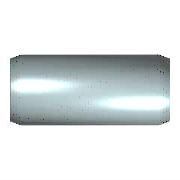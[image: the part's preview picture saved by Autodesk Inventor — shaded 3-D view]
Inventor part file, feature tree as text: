
AUTODESK INVENTOR PART (.ipt)
format: ipt  version: 2023.3 (Build 273359000, 359)  size: 163,328 bytes
history: native  units: mm (DEFAULTED — no unit token found)
features: sketch x5, extrude x3, plane x2, chamfer x1, hole x1, revolve x1
ambient origin geometry x8: Origin, YZ Plane, XZ Plane, XY Plane, X Axis, Y Axis, Z Axis, Center Point
bodies: Solid1 (feature_tree)
feature tree (13):
  extrude  "Körper"  Depth=16.0mm TaperAngle=0.0deg
  chamfer  "Skizze2"  Distance=0.5mm
  plane  "Arbeitsebene1"
  hole  "Bohrung1"  [1 undecoded]
  extrude  "Extrusion2"  TaperAngle=0.0deg  [1 undecoded]
  plane  "Arbeitsebene2"
  extrude  "Extrusion3"  TaperAngle=0.0deg  [1 undecoded]
  revolve  "Umdrehung1"
  sketch  "Skizze"  dims[d9=15.0deg d11=0.5mm d12=0.5mm d13=0.0mm d15=0.0mm d16=0.0mm d17=1.5mm d18=5.5mm d19=0.5mm d20=6.0mm d21=1.7mm d22=2.0mm d23=30.0deg d24=12.0mm d25=0.0mm d26=2.0mm d27=5.5mm d28=1.0mm d29=0.0mm d30=0.0mm d31=-1.5mm d32=3.0mm d33=5.0mm d34=0.5mm d35=0.0mm d36=1.0mm d37=1.0mm d38=0.75mm d39=90.0deg]
  sketch  "Skizze3"  dims[d1=3.0mm d2=16.0mm d3=0.0mm]
  sketch  "Skizze4"  dims[d4=0.5mm]
  sketch  "Skizze5"  dims[d5=15.0deg]
  sketch  "Skizze6"  dims[d8=0.5mm]
note: 3 required parameter values undecoded (feature->parameter linkage not recoverable at this tier; creation-order binding heuristic only, values carry confidence <= 0.55)
